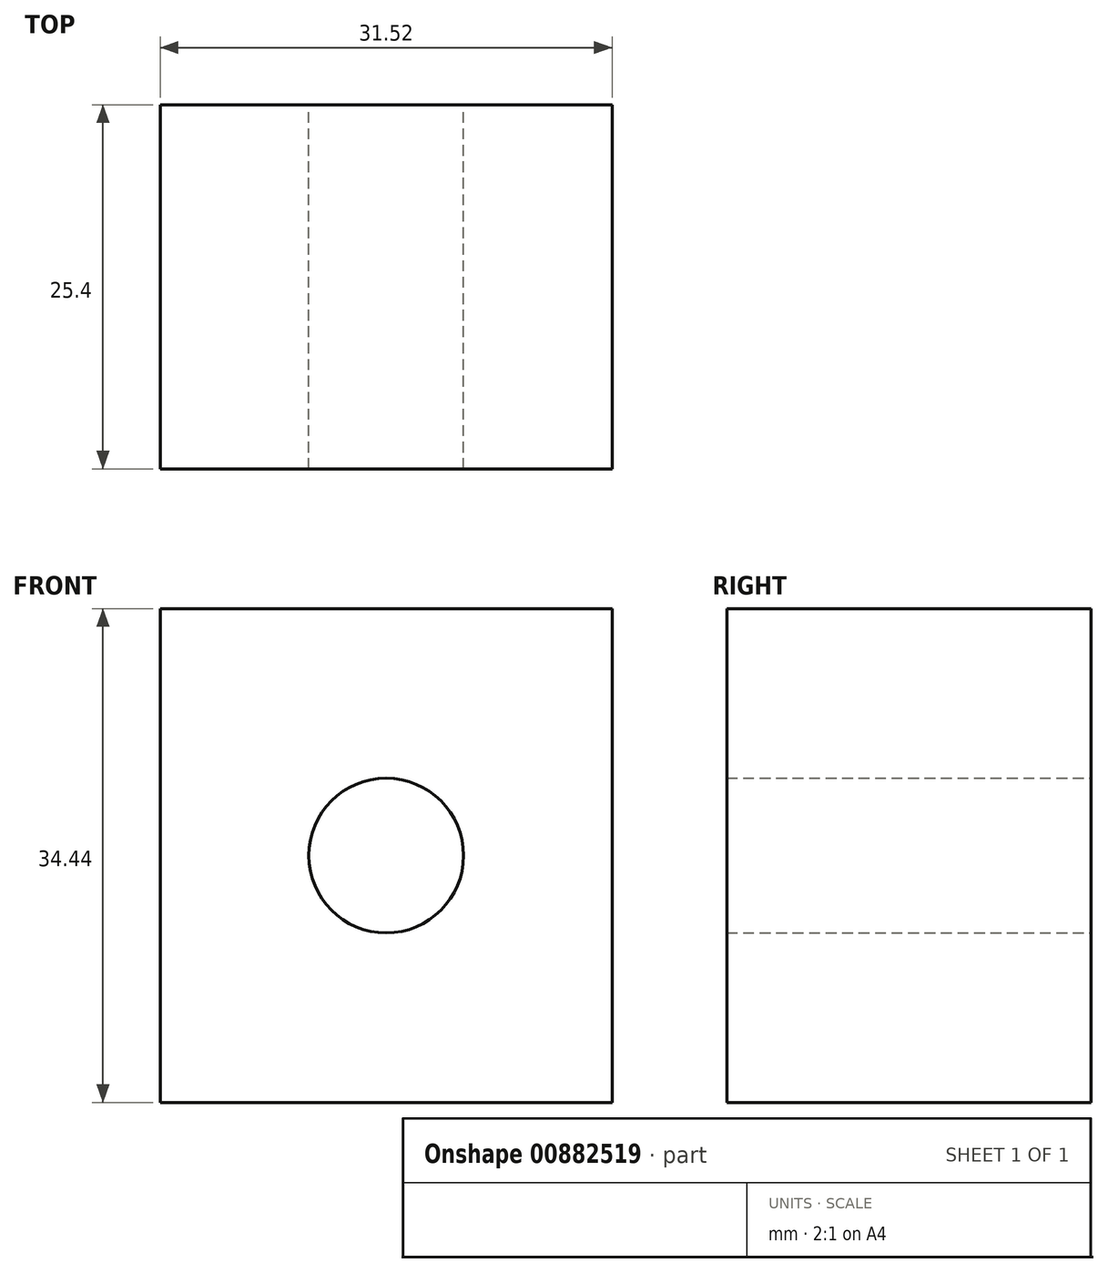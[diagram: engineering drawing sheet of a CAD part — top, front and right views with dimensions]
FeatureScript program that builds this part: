
annotation { "Feature Type Name" : "Feature", "Feature Type Description" : "" }
export const myFeature = defineFeature(function(context is Context, id is Id, definition is map)
    precondition{}
    {
        {
            var Q0;
            Q0=qCreatedBy(makeId("Front.planeOp"),FACE);
            var sketch = newSketch(context, id + "F0", { "sketchPlane" : qUnion([Q0])});
            skLineSegment(sketch, "E0.bottom", {"start": v(-15.76, 17.22) * mm, "end": v(15.76, 17.22) * mm});
            skLineSegment(sketch, "E0.top", {"start": v(-15.76, -17.22) * mm, "end": v(15.76, -17.22) * mm});
            skLineSegment(sketch, "E0.left", {"start": v(-15.76, 17.22) * mm, "end": v(-15.76, -17.22) * mm});
            skLineSegment(sketch, "E0.right", {"start": v(15.76, 17.22) * mm, "end": v(15.76, -17.22) * mm});
            skPoint(sketch, "E0.middle", {"position": v(0, 0) * mm});
            skCircle(sketch, "E1", {"center": v(0, 0) * mm, "radius": 5.4 * mm});
            skSolve(sketch);
        }
        {
            var Q0;
            Q0=makeQuery(id+"F0.imprint","IMPRINT",FACE,{"disambiguationData":[TD([[makeQuery(id+"F0.imprint","IMPRINT",EDGE,{"derivedFrom":sQuery(id+"F0.wireOp",EDGE,"E0.bottom")}),-1.0]])]});
            extrude(context, id + "F1", {"entities" : qUnion([Q0]), "depth" : 25.4 * mm, "offsetDistance" : 25.4 * mm});
        }
        {
            var Q0;
            Q0=qCreatedBy(makeId("Front.planeOp"),FACE);
            var sketch = newSketch(context, id + "F2", { "sketchPlane" : qUnion([Q0])});
            skCircle(sketch, "E2", {"center": v(0, 0) * mm, "radius": 5.61 * mm});
            skSolve(sketch);
        }
        {
            var Q0;
            Q0=qCreatedBy(makeId("Front.planeOp"),FACE);
            var sketch = newSketch(context, id + "F3", { "sketchPlane" : qUnion([Q0])});
            skCircle(sketch, "E3", {"center": v(0, 0) * mm, "radius": 6.6 * mm});
            skSolve(sketch);
        }
        {
            var Q0;
            Q0=sQuery(id+"F3.wireOp",EDGE,"E3");
            var Q1;
            Q1=sQuery(id+"F2.wireOp",EDGE,"E2");
            extrude(context, id + "F4", {"bodyType" : ToolBodyType.SURFACE, "surfaceEntities" : qUnion([Q0, Q1]), "oppositeDirection" : true, "depth" : 19.8 * mm, "offsetDistance" : 25.4 * mm});
        }
    });
